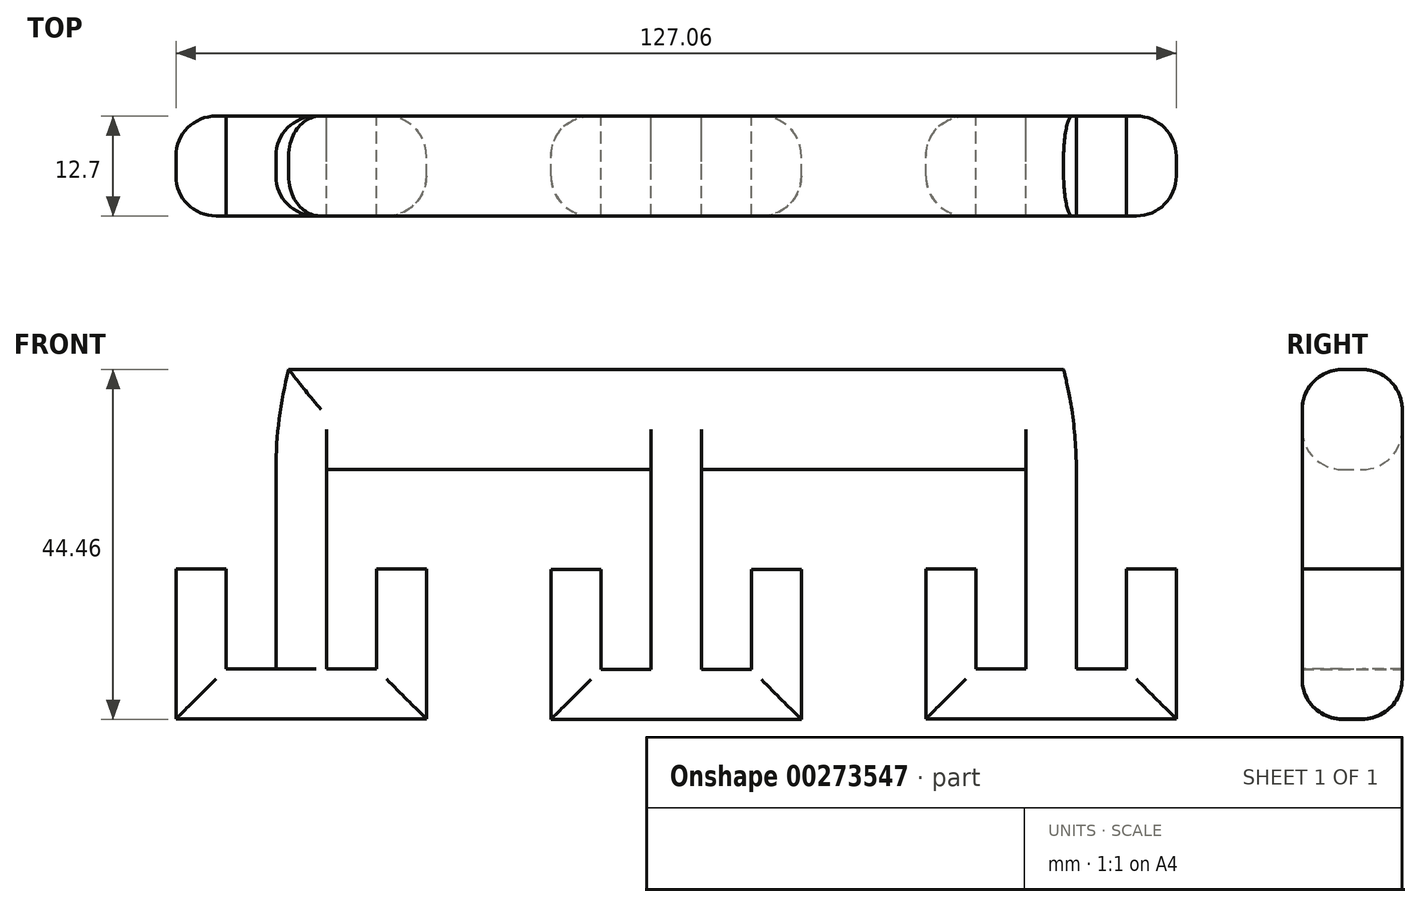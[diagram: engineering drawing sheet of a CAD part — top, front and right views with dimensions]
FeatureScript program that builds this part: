
annotation { "Feature Type Name" : "Feature", "Feature Type Description" : "" }
export const myFeature = defineFeature(function(context is Context, id is Id, definition is map)
    precondition{}
    {
        {
            var Q0;
            Q0=qCreatedBy(makeId("Front.planeOp"),FACE);
            var sketch = newSketch(context, id + "F0", { "sketchPlane" : qUnion([Q0])});
            skLineSegment(sketch, "E0.top", {"start": v(3.2, -15.88) * mm, "end": v(-3.2, -15.88) * mm});
            skLineSegment(sketch, "E0.left", {"start": v(3.2, 15.87) * mm, "end": v(3.2, -15.87) * mm});
            skLineSegment(sketch, "E0.right", {"start": v(-3.2, 15.88) * mm, "end": v(-3.2, -15.87) * mm});
            skPoint(sketch, "E0.middle", {"position": v(0, 0) * mm});
            skLineSegment(sketch, "E1", {"start": v(-9.55, -15.88) * mm, "end": v(-9.55, 3.18) * mm});
            skLineSegment(sketch, "E2", {"start": v(-9.55, 3.17) * mm, "end": v(-15.9, 3.17) * mm});
            skLineSegment(sketch, "E3", {"start": v(-15.9, 3.18) * mm, "end": v(-15.9, -15.88) * mm});
            skLineSegment(sketch, "E4", {"start": v(-15.9, -15.88) * mm, "end": v(15.9, -15.88) * mm});
            skLineSegment(sketch, "E5", {"start": v(15.9, -15.87) * mm, "end": v(15.9, 3.18) * mm});
            skLineSegment(sketch, "E6", {"start": v(15.9, 3.18) * mm, "end": v(9.55, 3.17) * mm});
            skLineSegment(sketch, "E7", {"start": v(9.55, 3.18) * mm, "end": v(9.55, -9.52) * mm});
            skLineSegment(sketch, "E8", {"start": v(-9.55, -9.52) * mm, "end": v(-3.2, -9.52) * mm});
            skLineSegment(sketch, "E9", {"start": v(9.55, -9.53) * mm, "end": v(3.2, -9.53) * mm});
            skLineSegment(sketch, "E10", {"start": v(0, 0) * mm, "end": v(0, 15.87) * mm});
            skLineSegment(sketch, "E11", {"start": v(-3.2, 15.88) * mm, "end": v(-63.53, 15.88) * mm});
            skLineSegment(sketch, "E12", {"start": v(3.2, 15.88) * mm, "end": v(63.53, 15.87) * mm});
            skArc(sketch, "E13", {"start": v(-63.53, 15.87) * mm, "mid": v(0, 79.4) * mm, "end": v(63.53, 15.88) * mm});
            skArc(sketch, "E14", {"start": v(-50.83, 15.88) * mm, "mid": v(0, 66.7) * mm, "end": v(50.83, 15.88) * mm});
            skLineSegment(sketch, "E15", {"start": v(-49.22, 28.58) * mm, "end": v(49.22, 28.57) * mm});
            skLineSegment(sketch, "E16.1.0.0", {"start": v(50.83, 15.94) * mm, "end": v(50.83, -15.81) * mm});
            skLineSegment(sketch, "E16.1.0.1", {"start": v(44.42, 15.94) * mm, "end": v(44.42, -15.81) * mm});
            skLineSegment(sketch, "E16.1.0.2", {"start": v(57.18, 3.24) * mm, "end": v(57.18, -9.46) * mm});
            skLineSegment(sketch, "E16.1.0.3", {"start": v(63.53, -15.81) * mm, "end": v(63.53, 3.24) * mm});
            skLineSegment(sketch, "E16.1.0.4", {"start": v(31.72, -15.81) * mm, "end": v(63.53, -15.81) * mm});
            skLineSegment(sketch, "E16.1.0.5", {"start": v(57.18, -9.46) * mm, "end": v(50.83, -9.46) * mm});
            skLineSegment(sketch, "E16.1.0.6", {"start": v(38.07, -9.46) * mm, "end": v(44.42, -9.46) * mm});
            skLineSegment(sketch, "E16.1.0.7", {"start": v(38.07, -15.81) * mm, "end": v(38.07, 3.24) * mm});
            skLineSegment(sketch, "E16.1.0.8", {"start": v(38.07, 3.24) * mm, "end": v(31.72, 3.24) * mm});
            skLineSegment(sketch, "E16.1.0.9", {"start": v(31.72, 3.24) * mm, "end": v(31.72, -15.81) * mm});
            skLineSegment(sketch, "E16.1.0.10", {"start": v(63.53, 3.24) * mm, "end": v(57.18, 3.24) * mm});
            skLineSegment(sketch, "E17.MirrorCS", {"start": v(-44.42, 15.94) * mm, "end": v(-44.42, -15.81) * mm});
            skLineSegment(sketch, "E18.MirrorCS", {"start": v(-50.83, 15.94) * mm, "end": v(-50.83, -15.81) * mm});
            skLineSegment(sketch, "E19.MirrorCS", {"start": v(-38.07, -9.46) * mm, "end": v(-44.42, -9.46) * mm});
            skLineSegment(sketch, "E20.MirrorCS", {"start": v(-31.72, 3.24) * mm, "end": v(-31.72, -15.81) * mm});
            skLineSegment(sketch, "E21.MirrorCS", {"start": v(-38.07, -15.81) * mm, "end": v(-38.07, 3.24) * mm});
            skLineSegment(sketch, "E22.MirrorCS", {"start": v(-38.07, 3.24) * mm, "end": v(-31.72, 3.24) * mm});
            skLineSegment(sketch, "E23.MirrorCS", {"start": v(-31.72, -15.81) * mm, "end": v(-63.53, -15.81) * mm});
            skLineSegment(sketch, "E24.MirrorCS", {"start": v(-63.53, -15.81) * mm, "end": v(-63.53, 3.24) * mm});
            skLineSegment(sketch, "E25.MirrorCS", {"start": v(-63.53, 3.24) * mm, "end": v(-57.18, 3.24) * mm});
            skLineSegment(sketch, "E26.MirrorCS", {"start": v(-57.18, 3.24) * mm, "end": v(-57.18, -9.46) * mm});
            skLineSegment(sketch, "E27.MirrorCS", {"start": v(-57.18, -9.46) * mm, "end": v(-50.83, -9.46) * mm});
            skSolve(sketch);
        }
        {
            var Q0;
            {var subQ10=sQuery(id+"F0.wireOp",EDGE,"E15");Q0=makeQuery(id+"F0.imprint","IMPRINT",FACE,{"disambiguationData":[TD([[makeQuery(id+"F0.imprint","IMPRINT",EDGE,{"derivedFrom":subQ10}),-1.0]])]});}
            var Q1;
            {var subQ6=sQuery(id+"F0.wireOp",EDGE,"E13");Q1=makeQuery(id+"F0.imprint","IMPRINT",FACE,{"disambiguationData":[TD([[makeQuery(id+"F0.imprint","IMPRINT",EDGE,{"derivedFrom":subQ6}),-1.0]])]});}
            var Q2;
            {var subQ0=sQuery(id+"F0.wireOp",EDGE,"E5");Q2=makeQuery(id+"F0.imprint","IMPRINT",FACE,{"disambiguationData":[TD([[makeQuery(id+"F0.imprint","IMPRINT",EDGE,{"derivedFrom":subQ0}),1.0]])]});}
            var Q3;
            {var subQ1=sQuery(id+"F0.wireOp",EDGE,"E2");Q3=makeQuery(id+"F0.imprint","IMPRINT",FACE,{"disambiguationData":[TD([[makeQuery(id+"F0.imprint","IMPRINT",EDGE,{"derivedFrom":subQ1}),1.0]])]});}
            var Q4;
            {var subQ3=sQuery(id+"F0.wireOp",EDGE,"E8");Q4=makeQuery(id+"F0.imprint","IMPRINT",FACE,{"disambiguationData":[TD([[makeQuery(id+"F0.imprint","IMPRINT",EDGE,{"derivedFrom":subQ3}),-1.0]])]});}
            var Q5;
            {var subQ1=sQuery(id+"F0.wireOp",EDGE,"E17.MirrorCS");var subQ6=sQuery(id+"F0.wireOp",EDGE,"E11");var subQ7=makeQuery(id+"F0.imprint","INTERSECT",VERTEX,{"derivedFrom":[subQ6,subQ1]});Q5=makeQuery(id+"F0.imprint","IMPRINT",FACE,{"disambiguationData":[TD([[makeQuery(id+"F0.imprint","IMPRINT",EDGE,{"disambiguationData":[TD([[subQ7,-1.0]])],"derivedFrom":subQ6}),1.0]])]});}
            var Q6;
            {var subQ5=sQuery(id+"F0.wireOp",EDGE,"E20.MirrorCS");Q6=makeQuery(id+"F0.imprint","IMPRINT",FACE,{"disambiguationData":[TD([[makeQuery(id+"F0.imprint","IMPRINT",EDGE,{"derivedFrom":subQ5}),-1.0]])]});}
            var Q7;
            {var subQ3=sQuery(id+"F0.wireOp",EDGE,"E19.MirrorCS");Q7=makeQuery(id+"F0.imprint","IMPRINT",FACE,{"disambiguationData":[TD([[makeQuery(id+"F0.imprint","IMPRINT",EDGE,{"derivedFrom":subQ3}),1.0]])]});}
            var Q8;
            {var subQ0=sQuery(id+"F0.wireOp",EDGE,"E24.MirrorCS");Q8=makeQuery(id+"F0.imprint","IMPRINT",FACE,{"disambiguationData":[TD([[makeQuery(id+"F0.imprint","IMPRINT",EDGE,{"derivedFrom":subQ0}),-1.0]])]});}
            var Q9;
            {var subQ0=sQuery(id+"F0.wireOp",EDGE,"E16.1.0.8");Q9=makeQuery(id+"F0.imprint","IMPRINT",FACE,{"disambiguationData":[TD([[makeQuery(id+"F0.imprint","IMPRINT",EDGE,{"derivedFrom":subQ0}),1.0]])]});}
            var Q10;
            {var subQ0=sQuery(id+"F0.wireOp",EDGE,"E16.1.0.1");var subQ2=sQuery(id+"F0.wireOp",EDGE,"E12");var subQ3=makeQuery(id+"F0.imprint","INTERSECT",VERTEX,{"derivedFrom":[subQ2,subQ0]});Q10=makeQuery(id+"F0.imprint","IMPRINT",FACE,{"disambiguationData":[TD([[makeQuery(id+"F0.imprint","IMPRINT",EDGE,{"disambiguationData":[TD([[subQ3,-1.0]])],"derivedFrom":subQ2}),-1.0]])]});}
            var Q11;
            {var subQ3=sQuery(id+"F0.wireOp",EDGE,"E16.1.0.6");Q11=makeQuery(id+"F0.imprint","IMPRINT",FACE,{"disambiguationData":[TD([[makeQuery(id+"F0.imprint","IMPRINT",EDGE,{"derivedFrom":subQ3}),-1.0]])]});}
            var Q12;
            Q12=makeQuery(id+"F0.imprint","IMPRINT",FACE,{"disambiguationData":[TD([[makeQuery(id+"F0.imprint","IMPRINT",EDGE,{"derivedFrom":sQuery(id+"F0.wireOp",EDGE,"E16.1.0.2")}),1.0]])]});
            extrude(context, id + "F1", {"entities" : qUnion([Q0, Q1, Q2, Q3, Q4, Q5, Q6, Q7, Q8, Q9, Q10, Q11, Q12]), "depth" : 12.7 * mm});
        }
        {
            var Q0;
            Q0=makeQuery(id+"F1.opExtrude","CAP_EDGE",EDGE,{"disambiguationData":[OSD([sQuery(id+"F0.wireOp",EDGE,"E13")])],"isStart":false});
            var Q1;
            Q1=makeQuery(id+"F1.opExtrude","CAP_EDGE",EDGE,{"disambiguationData":[OSD([sQuery(id+"F0.wireOp",EDGE,"E13")])],"isStart":true});
            var Q2;
            Q2=makeQuery(id+"F1.opExtrude","CAP_EDGE",EDGE,{"disambiguationData":[OSD([sQuery(id+"F0.wireOp",EDGE,"E11")])],"isStart":true});
            var Q3;
            Q3=makeQuery(id+"F1.opExtrude","CAP_EDGE",EDGE,{"disambiguationData":[OSD([sQuery(id+"F0.wireOp",EDGE,"E12")])],"isStart":true});
            var Q4;
            Q4=makeQuery(id+"F1.opExtrude","CAP_EDGE",EDGE,{"disambiguationData":[OSD([sQuery(id+"F0.wireOp",EDGE,"E11")])],"isStart":false});
            var Q5;
            Q5=makeQuery(id+"F1.opExtrude","CAP_EDGE",EDGE,{"disambiguationData":[OSD([sQuery(id+"F0.wireOp",EDGE,"E12")])],"isStart":false});
            var Q6;
            Q6=makeQuery(id+"F1.opExtrude","CAP_EDGE",EDGE,{"disambiguationData":[OSD([sQuery(id+"F0.wireOp",EDGE,"E5")])],"isStart":false});
            var Q7;
            Q7=makeQuery(id+"F1.opExtrude","CAP_EDGE",EDGE,{"disambiguationData":[OSD([sQuery(id+"F0.wireOp",EDGE,"E5")])],"isStart":true});
            var Q8;
            Q8=makeQuery(id+"F1.opExtrude","CAP_EDGE",EDGE,{"disambiguationData":[OSD([sQuery(id+"F0.wireOp",EDGE,"E3")])],"isStart":false});
            var Q9;
            Q9=makeQuery(id+"F1.opExtrude","CAP_EDGE",EDGE,{"disambiguationData":[OSD([sQuery(id+"F0.wireOp",EDGE,"E3")])],"isStart":true});
            var Q10;
            Q10=makeQuery(id+"F1.opExtrude","CAP_EDGE",EDGE,{"disambiguationData":[OSD([sQuery(id+"F0.wireOp",EDGE,"E4")])],"isStart":false});
            var Q11;
            Q11=makeQuery(id+"F1.opExtrude","CAP_EDGE",EDGE,{"disambiguationData":[OSD([sQuery(id+"F0.wireOp",EDGE,"E4")])],"isStart":true});
            var Q12;
            Q12=makeQuery(id+"F1.opExtrude","CAP_EDGE",EDGE,{"disambiguationData":[OSD([sQuery(id+"F0.wireOp",EDGE,"E16.1.0.4")])],"isStart":true});
            var Q13;
            Q13=makeQuery(id+"F1.opExtrude","CAP_EDGE",EDGE,{"disambiguationData":[OSD([sQuery(id+"F0.wireOp",EDGE,"E16.1.0.9")])],"isStart":true});
            var Q14;
            Q14=makeQuery(id+"F1.opExtrude","CAP_EDGE",EDGE,{"disambiguationData":[OSD([sQuery(id+"F0.wireOp",EDGE,"E16.1.0.9")])],"isStart":false});
            var Q15;
            Q15=makeQuery(id+"F1.opExtrude","CAP_EDGE",EDGE,{"disambiguationData":[OSD([sQuery(id+"F0.wireOp",EDGE,"E16.1.0.3")])],"isStart":true});
            var Q16;
            Q16=makeQuery(id+"F1.opExtrude","CAP_EDGE",EDGE,{"disambiguationData":[OSD([sQuery(id+"F0.wireOp",EDGE,"E16.1.0.3")])],"isStart":false});
            var Q17;
            Q17=makeQuery(id+"F1.opExtrude","CAP_EDGE",EDGE,{"disambiguationData":[OSD([sQuery(id+"F0.wireOp",EDGE,"E20.MirrorCS")])],"isStart":false});
            var Q18;
            Q18=makeQuery(id+"F1.opExtrude","CAP_EDGE",EDGE,{"disambiguationData":[OSD([sQuery(id+"F0.wireOp",EDGE,"E23.MirrorCS")])],"isStart":false});
            var Q19;
            Q19=makeQuery(id+"F1.opExtrude","CAP_EDGE",EDGE,{"disambiguationData":[OSD([sQuery(id+"F0.wireOp",EDGE,"E20.MirrorCS")])],"isStart":true});
            var Q20;
            Q20=makeQuery(id+"F1.opExtrude","CAP_EDGE",EDGE,{"disambiguationData":[OSD([sQuery(id+"F0.wireOp",EDGE,"E23.MirrorCS")])],"isStart":true});
            var Q21;
            Q21=makeQuery(id+"F1.opExtrude","CAP_EDGE",EDGE,{"disambiguationData":[OSD([sQuery(id+"F0.wireOp",EDGE,"E24.MirrorCS")])],"isStart":true});
            var Q22;
            Q22=makeQuery(id+"F1.opExtrude","CAP_EDGE",EDGE,{"disambiguationData":[OSD([sQuery(id+"F0.wireOp",EDGE,"E24.MirrorCS")])],"isStart":false});
            var Q23;
            Q23=makeQuery(id+"F1.opExtrude","CAP_EDGE",EDGE,{"disambiguationData":[OSD([sQuery(id+"F0.wireOp",EDGE,"E16.1.0.4")])],"isStart":false});
            var Q24;
            {var subQ0=sQuery(id+"F0.wireOp",EDGE,"E15");var subQ1=sQuery(id+"F0.wireOp",EDGE,"E14");Q24=makeQuery(id+"F1.opExtrude","CAP_EDGE",EDGE,{"disambiguationData":[OSD([subQ1]),TDD([makeQuery(id+"F0.imprint","IMPRINT",EDGE,{"disambiguationData":[TD([[makeQuery(id+"F0.imprint","INTERSECT",VERTEX,{"disambiguationData":[OD(0.0)],"derivedFrom":[subQ1,subQ0]}),-1.0]])],"derivedFrom":subQ1})])],"isStart":false});}
            var Q25;
            {var subQ0=sQuery(id+"F0.wireOp",EDGE,"E15");var subQ1=sQuery(id+"F0.wireOp",EDGE,"E14");Q25=makeQuery(id+"F1.opExtrude","CAP_EDGE",EDGE,{"disambiguationData":[OSD([subQ1]),TDD([makeQuery(id+"F0.imprint","IMPRINT",EDGE,{"disambiguationData":[TD([[makeQuery(id+"F0.imprint","INTERSECT",VERTEX,{"disambiguationData":[OD(0.0)],"derivedFrom":[subQ1,subQ0]}),-1.0]])],"derivedFrom":subQ1})])],"isStart":true});}
            var Q26;
            Q26=makeQuery(id+"F1.opExtrude","CAP_EDGE",EDGE,{"disambiguationData":[OSD([sQuery(id+"F0.wireOp",EDGE,"E15")])],"isStart":false});
            var Q27;
            Q27=makeQuery(id+"F1.opExtrude","CAP_EDGE",EDGE,{"disambiguationData":[OSD([sQuery(id+"F0.wireOp",EDGE,"E15")])],"isStart":true});
            fillet(context, id + "F2", {"entities" : qUnion([Q0, Q1, Q2, Q3, Q4, Q5, Q6, Q7, Q8, Q9, Q10, Q11, Q12, Q13, Q14, Q15, Q16, Q17, Q18, Q19, Q20, Q21, Q22, Q23, Q24, Q25, Q26, Q27]), "radius" : 5.08 * mm, "tangentPropagation" : true, "allowEdgeOverflow" : false});
        }
    });
